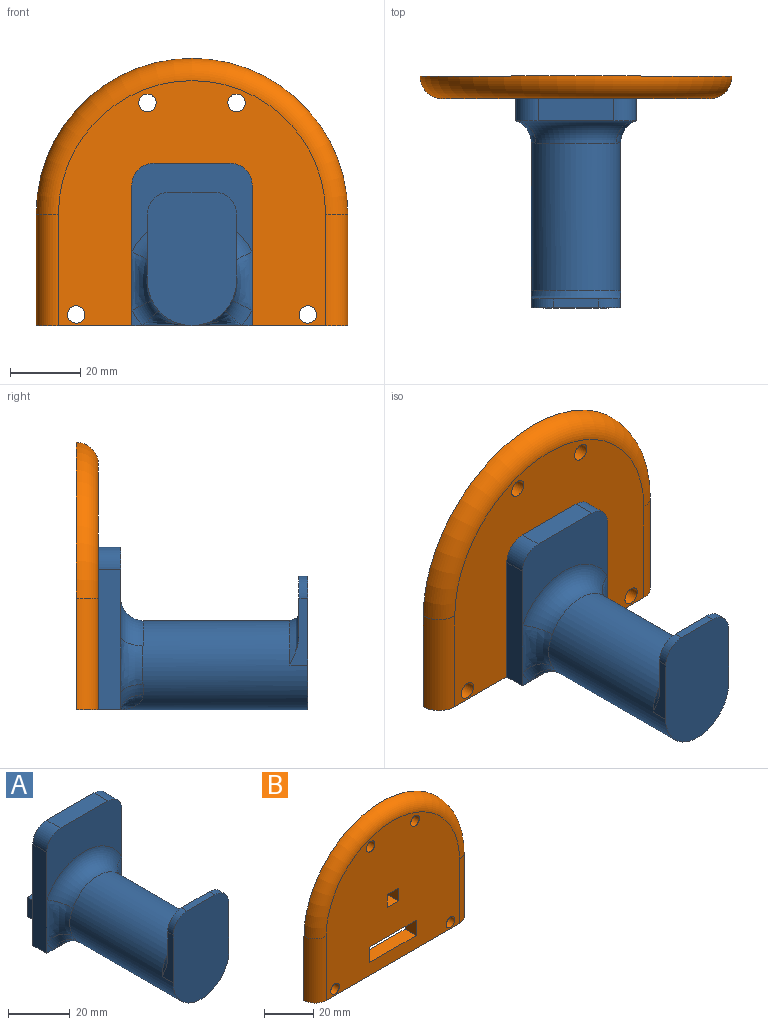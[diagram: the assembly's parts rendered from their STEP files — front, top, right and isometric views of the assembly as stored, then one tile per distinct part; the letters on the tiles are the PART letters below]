
ASSEMBLY  parts=2 mates=1
PART A: 36 faces, bbox 46.7x66.8x50.3 mm
  f0: plane 4.4x2.95mm, normal (0,-1,0), area 5.8mm2, adj f2,f28,f30
  f1: plane 34.29x25.35mm, normal (0,-1,0), area 588mm2, adj f2,f3,f6,f7,f8,f32
  f2: plane 40.24x6.58mm, normal (-1,0,0), area 254mm2, adj f0,f1,f5,f7,f28,f31
  f3: plane 40.24x6.58mm, normal (1,0,0), area 254mm2, adj f1,f4,f5,f8,f28,f33
  f4: plane 4.4x2.95mm, normal (0,-1,0), area 5.8mm2, adj f3,f28,f34
  f5: plane 46.36x34.29mm, normal (0,1,0), area 1328.7mm2, adj f2,f3,f6,f7,f8,f9,f10,f11
  f6: plane 21.59x6.35mm, normal (0,0,1), area 137.1mm2, adj f1,f5,f7,f8
  f7: cylinder r=6.35mm len=6.35mm, axis (0,-1,0), area 63.3mm2, adj f1,f2,f5,f6
  f8: cylinder r=6.35mm len=6.35mm, axis (0,1,0), area 63.3mm2, adj f1,f3,f5,f6
  f9: plane 6.35x6.35mm, normal (0,0,-1), area 40.3mm2, adj f5,f10,f12,f13
  f10: plane 6.35x6.35mm, normal (-1,0,0), area 40.3mm2, adj f5,f9,f11,f13
  f11: plane 6.35x6.35mm, normal (0,0,1), area 40.3mm2, adj f5,f10,f12,f13
  f12: plane 6.35x6.35mm, normal (1,0,0), area 40.3mm2, adj f5,f9,f11,f13
  f13: plane 6.35x6.35mm, normal (0,1,0), area 40.3mm2, adj f9,f10,f11,f12
  f14: plane 26.67x6.35mm, normal (0,0,1), area 169.4mm2, adj f5,f15,f17,f18
  f15: plane 7.62x6.35mm, normal (1,0,0), area 48.4mm2, adj f5,f14,f16,f18
  f16: plane 26.67x6.35mm, normal (0,0,-1), area 169.4mm2, adj f5,f15,f17,f18
  f17: plane 7.62x6.35mm, normal (-1,0,0), area 48.4mm2, adj f5,f14,f16,f18
  f18: plane 26.67x7.62mm, normal (0,1,0), area 203.2mm2, adj f14,f15,f16,f17
  f19: cylinder r=12.7mm len=53.34mm, axis (0,1,0), area 3598.9mm2, adj f21,f23,f24,f27,f29,f30,f31,f32
  f20: plane 25.4x16.98mm, normal (0,1,0), area 292.1mm2, adj f21,f22,f23,f25,f26,f27
  f21: plane 19.67x5.7mm, normal (1,0,0), area 56.5mm2, adj f19,f20,f24,f25,f27
  f22: plane 12.7x2.54mm, normal (0,0,1), area 32.3mm2, adj f20,f24,f25,f26
  f23: plane 19.67x5.7mm, normal (-1,0,0), area 56.5mm2, adj f19,f20,f24,f26,f27
  f24: plane 38.1x25.4mm, normal (0,-1,0), area 881.2mm2, adj f19,f21,f22,f23,f25,f26
  f25: cylinder r=6.35mm len=6.35mm, axis (0,-1,0), area 25.3mm2, adj f20,f21,f22,f24
  f26: cylinder r=6.35mm len=6.35mm, axis (0,1,0), area 25.3mm2, adj f20,f22,f23,f24
  f27: torus R=15.24mm, axis (0,-1,0), area 137.9mm2, adj f19,f20,f21,f23
  f28: plane 35.05x7.11mm, normal (0,0,-1), area 217.7mm2, adj f0,f2,f3,f4,f5,f29,f35
  f29: bspline ~14.73x6.73mm, area 54mm2, adj f19,f28,f30
  f30: torus R=19.05mm, axis (0,-1,0), area 41.7mm2, adj f0,f19,f29,f31
  f31: bspline ~18.87x7.05mm, area 113.6mm2, adj f2,f19,f30,f32
  f32: torus R=19.05mm, axis (0,-1,0), area 335.2mm2, adj f1,f19,f31,f33
  f33: bspline ~18.87x7.05mm, area 113.6mm2, adj f3,f19,f32,f34
  f34: torus R=19.05mm, axis (0,-1,0), area 41.7mm2, adj f4,f19,f33,f35
  f35: bspline ~14.73x6.73mm, area 54mm2, adj f19,f28,f34
PART B: 18 faces, bbox 96.2x6.4x79.9 mm
  f0: plane 76.2x69.85mm, normal (0,-1,0), area 4378.1mm2, adj f2,f3,f4,f5,f6,f7,f8,f9
  f1: plane 88.9x76.2mm, normal (0,1,0), area 5604.7mm2, adj f2,f3,f4,f5,f6,f7,f8,f9
  f2: plane 88.9x6.35mm, normal (0,0,-1), area 547.2mm2, adj f0,f1,f3,f5
  f3: cylinder r=6.35mm len=31.75mm, axis (0,0,1), area 316.7mm2, adj f0,f1,f2,f4
  f4: torus R=38.1mm, axis (0,-1,0), area 1320.6mm2, adj f0,f1,f3,f5
  f5: cylinder r=6.35mm len=31.75mm, axis (0,0,-1), area 316.7mm2, adj f0,f1,f2,f4
  f6: cylinder r=2.49mm len=6.35mm, axis (0,-1,0), area 99.3mm2, adj f0,f1
  f7: cylinder r=2.49mm len=6.35mm, axis (0,-1,0), area 99.3mm2, adj f0,f1
  f8: cylinder r=2.49mm len=6.35mm, axis (0,-1,0), area 99.3mm2, adj f0,f1
  f9: cylinder r=2.49mm len=6.35mm, axis (0,-1,0), area 99.3mm2, adj f0,f1
  f10: plane 26.67x6.35mm, normal (0,0,-1), area 169.4mm2, adj f0,f1,f11,f13
  f11: plane 7.62x6.35mm, normal (1,0,0), area 48.4mm2, adj f0,f1,f10,f12
  f12: plane 26.67x6.35mm, normal (0,0,1), area 169.4mm2, adj f0,f1,f11,f13
  f13: plane 7.62x6.35mm, normal (-1,0,0), area 48.4mm2, adj f0,f1,f10,f12
  f14: plane 6.35x6.35mm, normal (0,0,-1), area 40.3mm2, adj f0,f1,f15,f17
  f15: plane 6.35x6.35mm, normal (1,0,0), area 40.3mm2, adj f0,f1,f14,f16
  f16: plane 6.35x6.35mm, normal (0,0,1), area 40.3mm2, adj f0,f1,f15,f17
  f17: plane 6.35x6.35mm, normal (-1,0,0), area 40.3mm2, adj f0,f1,f14,f16
PLACE A t=(0.09,-3.07,-17.06)mm
PLACE B t=(0.09,3.28,-6.26)mm fixed
MATE fastened B.f4 <-> A.f5  axis (0,-1,0) through (0.09,-3.07,-6.26)mm
